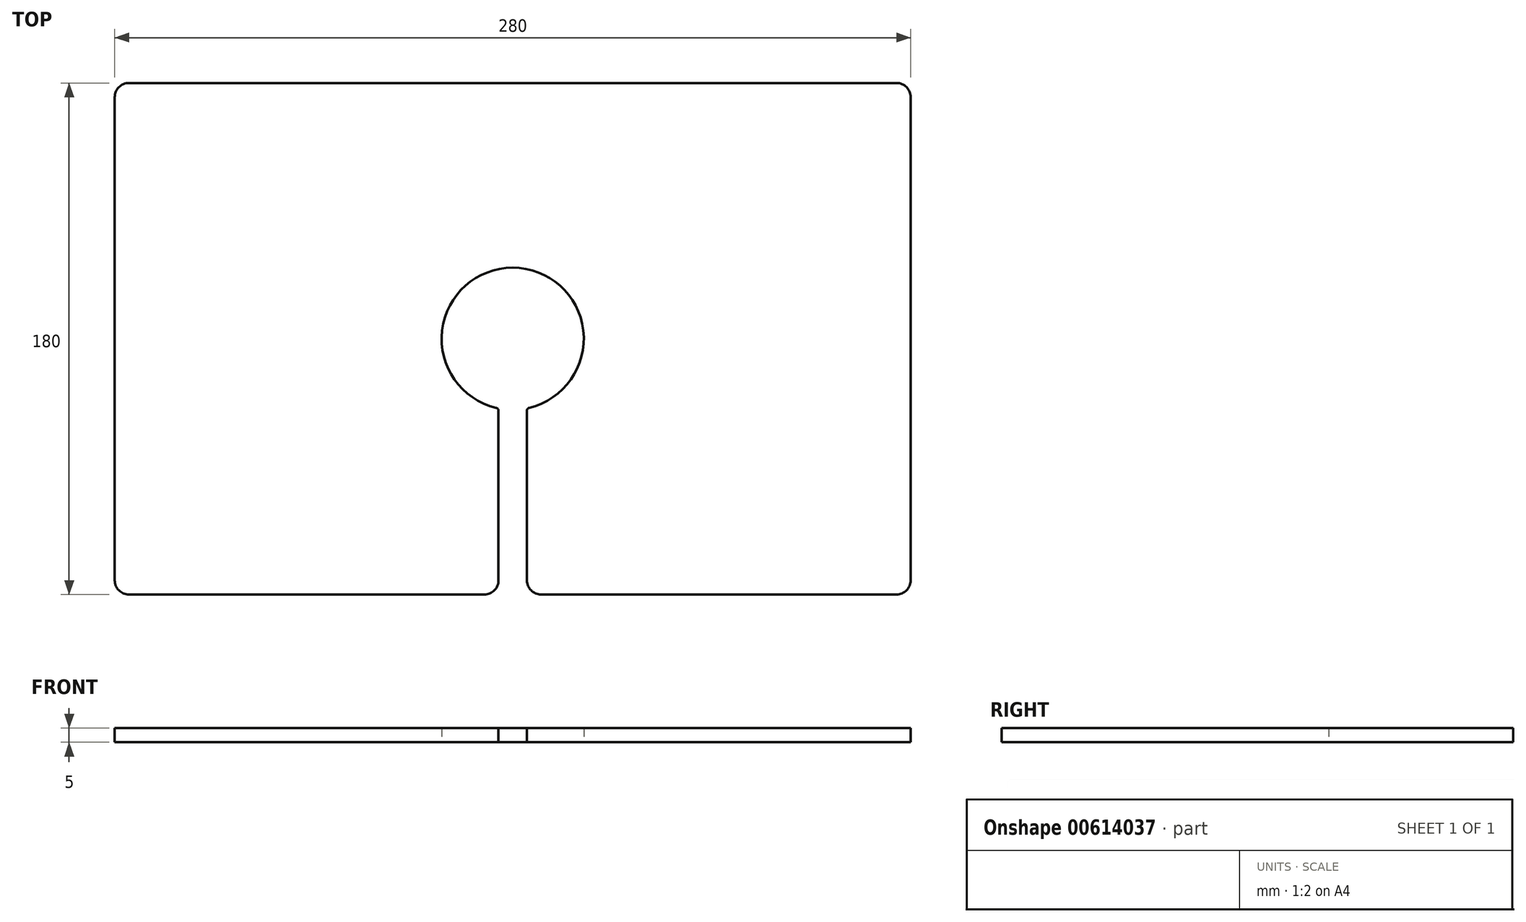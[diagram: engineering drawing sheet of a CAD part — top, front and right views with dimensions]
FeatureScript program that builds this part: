
annotation { "Feature Type Name" : "Feature", "Feature Type Description" : "" }
export const myFeature = defineFeature(function(context is Context, id is Id, definition is map)
    precondition{}
    {
        {
            var Q0;
            Q0=qCreatedBy(makeId("Top.planeOp"),FACE);
            var sketch = newSketch(context, id + "F0", { "sketchPlane" : qUnion([Q0])});
            skLineSegment(sketch, "E0", {"start": v(0, 0) * mm, "end": v(280, 0) * mm});
            skLineSegment(sketch, "E1", {"start": v(280, 0) * mm, "end": v(280, -180) * mm});
            skLineSegment(sketch, "E2", {"start": v(0, 0) * mm, "end": v(0, -180) * mm});
            skLineSegment(sketch, "E3", {"start": v(0, -180) * mm, "end": v(280, -180) * mm});
            skCircle(sketch, "E4", {"center": v(140, -90) * mm, "radius": 25 * mm});
            skLineSegment(sketch, "E5", {"start": v(140, -90) * mm, "end": v(140, 0) * mm});
            skLineSegment(sketch, "E6", {"start": v(140, -90) * mm, "end": v(140, -180) * mm});
            skLineSegment(sketch, "E7.bottom", {"start": v(145, -180) * mm, "end": v(135, -180) * mm});
            skLineSegment(sketch, "E7.top", {"start": v(145, -90) * mm, "end": v(135, -90) * mm});
            skLineSegment(sketch, "E7.left", {"start": v(145, -180) * mm, "end": v(145, -90) * mm});
            skLineSegment(sketch, "E7.right", {"start": v(135, -180) * mm, "end": v(135, -90) * mm});
            skPoint(sketch, "E7.middle", {"position": v(140, -135) * mm});
            skLineSegment(sketch, "E8", {"start": v(0, -95.55) * mm, "end": v(140, -95.55) * mm});
            skLineSegment(sketch, "E9", {"start": v(140, -95.55) * mm, "end": v(280, -95.55) * mm});
            skPoint(sketch, "E9.endSnap0", {"position": v(280, -90) * mm});
            skSolve(sketch);
        }
        {
            var Q0;
            {var subQ5=sQuery(id+"F0.wireOp",EDGE,"E2");var subQ6=sQuery(id+"F0.wireOp",EDGE,"E0");var subQ7=makeQuery(id+"F0.imprint","INTERSECT",VERTEX,{"derivedFrom":[subQ6,subQ5]});Q0=makeQuery(id+"F0.imprint","IMPRINT",FACE,{"disambiguationData":[TD([[makeQuery(id+"F0.imprint","IMPRINT",EDGE,{"disambiguationData":[TD([[subQ7,-1.0]])],"derivedFrom":subQ6}),-1.0]])]});}
            var Q1;
            {var subQ1=sQuery(id+"F0.wireOp",EDGE,"E0");var subQ7=sQuery(id+"F0.wireOp",EDGE,"E1");var subQ8=makeQuery(id+"F0.imprint","INTERSECT",VERTEX,{"derivedFrom":[subQ1,subQ7]});Q1=makeQuery(id+"F0.imprint","IMPRINT",FACE,{"disambiguationData":[TD([[makeQuery(id+"F0.imprint","IMPRINT",EDGE,{"disambiguationData":[TD([[subQ8,1.0]])],"derivedFrom":subQ1}),-1.0]])]});}
            var Q2;
            {var subQ5=sQuery(id+"F0.wireOp",EDGE,"E3");var subQ7=sQuery(id+"F0.wireOp",EDGE,"E1");var subQ9=makeQuery(id+"F0.imprint","INTERSECT",VERTEX,{"derivedFrom":[subQ7,subQ5]});Q2=makeQuery(id+"F0.imprint","IMPRINT",FACE,{"disambiguationData":[TD([[makeQuery(id+"F0.imprint","IMPRINT",EDGE,{"disambiguationData":[TD([[subQ9,1.0]])],"derivedFrom":subQ7}),-1.0]])]});}
            var Q3;
            {var subQ5=sQuery(id+"F0.wireOp",EDGE,"E3");var subQ7=sQuery(id+"F0.wireOp",EDGE,"E2");var subQ8=makeQuery(id+"F0.imprint","INTERSECT",VERTEX,{"derivedFrom":[subQ7,subQ5]});Q3=makeQuery(id+"F0.imprint","IMPRINT",FACE,{"disambiguationData":[TD([[makeQuery(id+"F0.imprint","IMPRINT",EDGE,{"disambiguationData":[TD([[subQ8,1.0]])],"derivedFrom":subQ7}),1.0]])]});}
            extrude(context, id + "F1", {"entities" : qUnion([Q0, Q1, Q2, Q3]), "depth" : 5 * mm, "offsetDistance" : 25 * mm});
        }
        {
            var Q0;
            Q0=makeQuery(id+"F1.opExtrude","SWEPT_EDGE",EDGE,{"disambiguationData":[OSD([sQuery(id+"F0.wireOp",EDGE,"E3"),sQuery(id+"F0.wireOp",EDGE,"E7.bottom"),sQuery(id+"F0.wireOp",EDGE,"E7.right")])]});
            var Q1;
            Q1=makeQuery(id+"F1.opExtrude","SWEPT_EDGE",EDGE,{"disambiguationData":[OSD([sQuery(id+"F0.wireOp",EDGE,"E3"),sQuery(id+"F0.wireOp",EDGE,"E7.bottom"),sQuery(id+"F0.wireOp",EDGE,"E7.left")])]});
            var Q2;
            Q2=makeQuery(id+"F1.opExtrude","SWEPT_EDGE",EDGE,{"disambiguationData":[OSD([sQuery(id+"F0.wireOp",EDGE,"E1"),sQuery(id+"F0.wireOp",EDGE,"E3")])]});
            var Q3;
            Q3=makeQuery(id+"F1.opExtrude","SWEPT_EDGE",EDGE,{"disambiguationData":[OSD([sQuery(id+"F0.wireOp",EDGE,"E2"),sQuery(id+"F0.wireOp",EDGE,"E3")])]});
            var Q4;
            Q4=makeQuery(id+"F1.opExtrude","SWEPT_EDGE",EDGE,{"disambiguationData":[OSD([sQuery(id+"F0.wireOp",EDGE,"E0"),sQuery(id+"F0.wireOp",EDGE,"E1")])]});
            var Q5;
            Q5=makeQuery(id+"F1.opExtrude","SWEPT_EDGE",EDGE,{"disambiguationData":[OSD([sQuery(id+"F0.wireOp",EDGE,"E0"),sQuery(id+"F0.wireOp",EDGE,"E2")])]});
            fillet(context, id + "F2", {"entities" : qUnion([Q0, Q1, Q2, Q3, Q4, Q5]), "radius" : 5 * mm, "tangentPropagation" : true, "allowEdgeOverflow" : false});
        }
        {
            var Q0;
            Q0=makeQuery(id+"F1.opExtrude","SWEPT_EDGE",EDGE,{"disambiguationData":[OSD([sQuery(id+"F0.wireOp",EDGE,"E4"),sQuery(id+"F0.wireOp",EDGE,"E7.right")])]});
            var Q1;
            Q1=makeQuery(id+"F1.opExtrude","SWEPT_EDGE",EDGE,{"disambiguationData":[OSD([sQuery(id+"F0.wireOp",EDGE,"E4"),sQuery(id+"F0.wireOp",EDGE,"E7.left")])]});
            fillet(context, id + "F3", {"entities" : qUnion([Q0, Q1]), "radius" : 1 * mm, "tangentPropagation" : true, "allowEdgeOverflow" : false});
        }
    });
